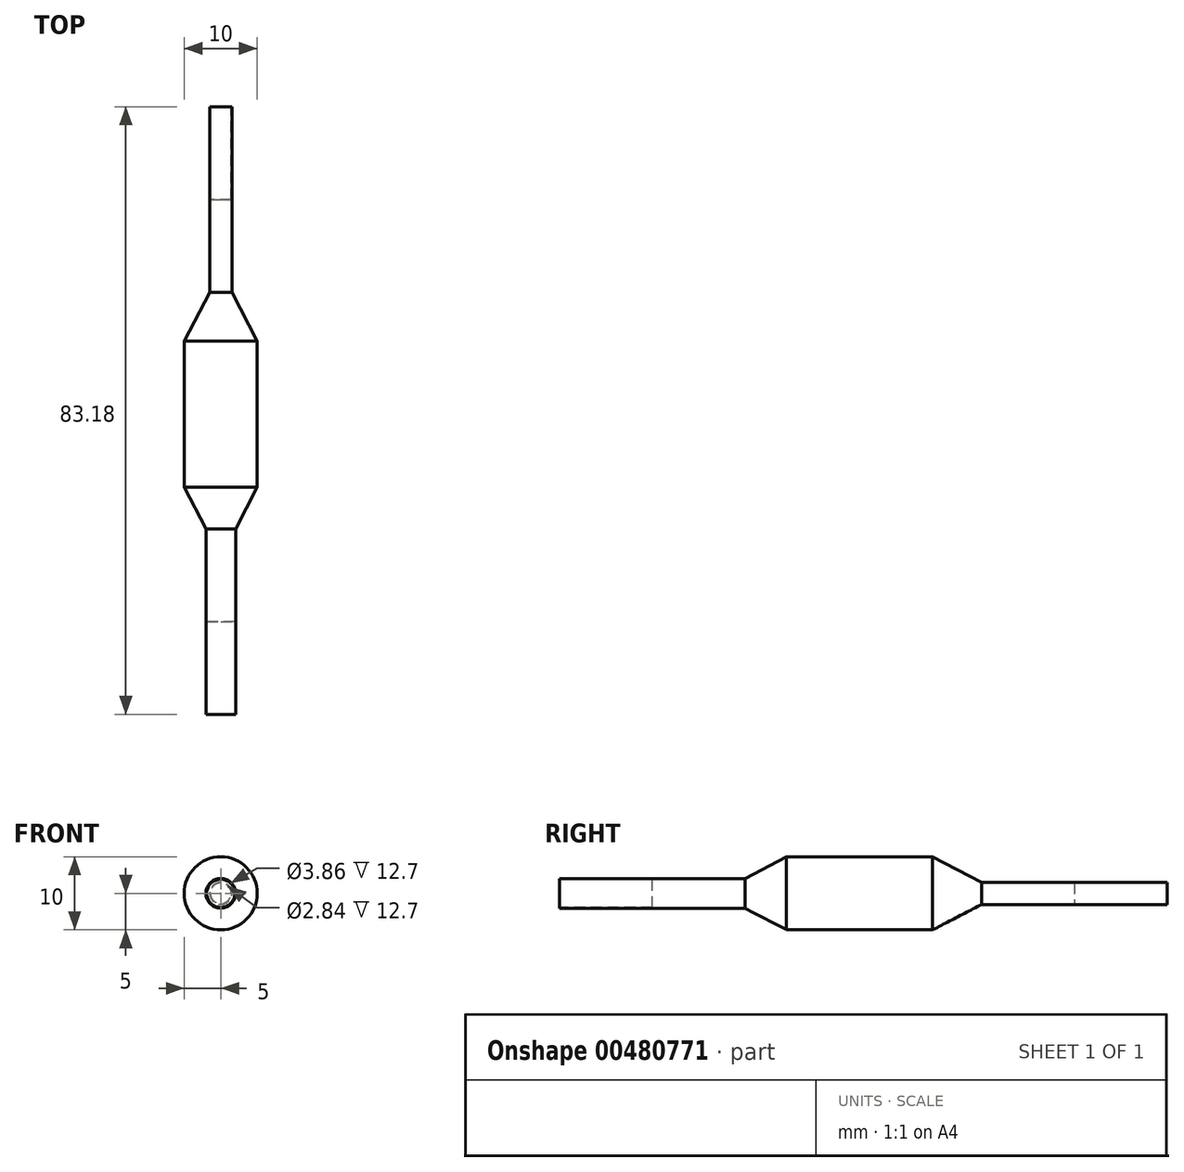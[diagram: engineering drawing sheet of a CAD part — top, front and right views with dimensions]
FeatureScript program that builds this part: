
annotation { "Feature Type Name" : "Feature", "Feature Type Description" : "" }
export const myFeature = defineFeature(function(context is Context, id is Id, definition is map)
    precondition{}
    {
        {
            var Q0;
            Q0=qCreatedBy(makeId("Right.planeOp"),FACE);
            var sketch = newSketch(context, id + "F0", { "sketchPlane" : qUnion([Q0])});
            skLineSegment(sketch, "E0", {"start": v(0, 0) * mm, "end": v(0, 2.03) * mm});
            skLineSegment(sketch, "E1", {"start": v(0, 2.03) * mm, "end": v(25.4, 2.03) * mm});
            skLineSegment(sketch, "E2", {"start": v(25.4, 2.03) * mm, "end": v(31.1, 5) * mm});
            skLineSegment(sketch, "E3", {"start": v(31.1, 5) * mm, "end": v(51.1, 5) * mm});
            skLineSegment(sketch, "E4", {"start": v(51.1, 5) * mm, "end": v(57.78, 1.52) * mm});
            skLineSegment(sketch, "E5", {"start": v(83.18, 1.52) * mm, "end": v(83.18, 0) * mm});
            skLineSegment(sketch, "E6", {"start": v(0, 0) * mm, "end": v(83.18, 0) * mm, "construction": true});
            skLineSegment(sketch, "E7", {"start": v(0, 0) * mm, "end": v(83.18, 0) * mm});
            skLineSegment(sketch, "E8", {"start": v(83.18, 1.52) * mm, "end": v(57.78, 1.52) * mm});
            skSolve(sketch);
        }
        {
            var Q0;
            Q0=qSketchRegion(id+"F0",true);
            var Q1;
            Q1=sQuery(id+"F0.wireOp",EDGE,"E6");
            revolve(context, id + "F1", {"entities" : qUnion([Q0]), "axis" : qUnion([Q1]), "revolveType" : RevolveType.FULL});
        }
        {
            var Q0;
            Q0=makeQuery(id+"F1.opRevolve","SWEPT_FACE",FACE,{"disambiguationData":[OSD([sQuery(id+"F0.wireOp",EDGE,"E0")])]});
            var sketch = newSketch(context, id + "F2", { "sketchPlane" : qUnion([Q0])});
            skCircle(sketch, "E9", {"center": v(0, 0) * mm, "radius": 1.93 * mm});
            skSolve(sketch);
        }
        {
            var Q0;
            Q0=qSketchRegion(id+"F2",true);
            extrude(context, id + "F3", {"entities" : qUnion([Q0]), "operationType" : NewBodyOperationType.REMOVE, "oppositeDirection" : true, "depth" : 12.7 * mm});
        }
        {
            var Q0;
            Q0=makeQuery(id+"F1.opRevolve","SWEPT_FACE",FACE,{"disambiguationData":[OSD([sQuery(id+"F0.wireOp",EDGE,"E5")])]});
            var sketch = newSketch(context, id + "F4", { "sketchPlane" : qUnion([Q0])});
            skCircle(sketch, "E10", {"center": v(0, 0) * mm, "radius": 1.42 * mm});
            skSolve(sketch);
        }
        {
            var Q0;
            Q0=qSketchRegion(id+"F4",true);
            extrude(context, id + "F5", {"entities" : qUnion([Q0]), "operationType" : NewBodyOperationType.REMOVE, "oppositeDirection" : true, "depth" : 12.7 * mm});
        }
    });
